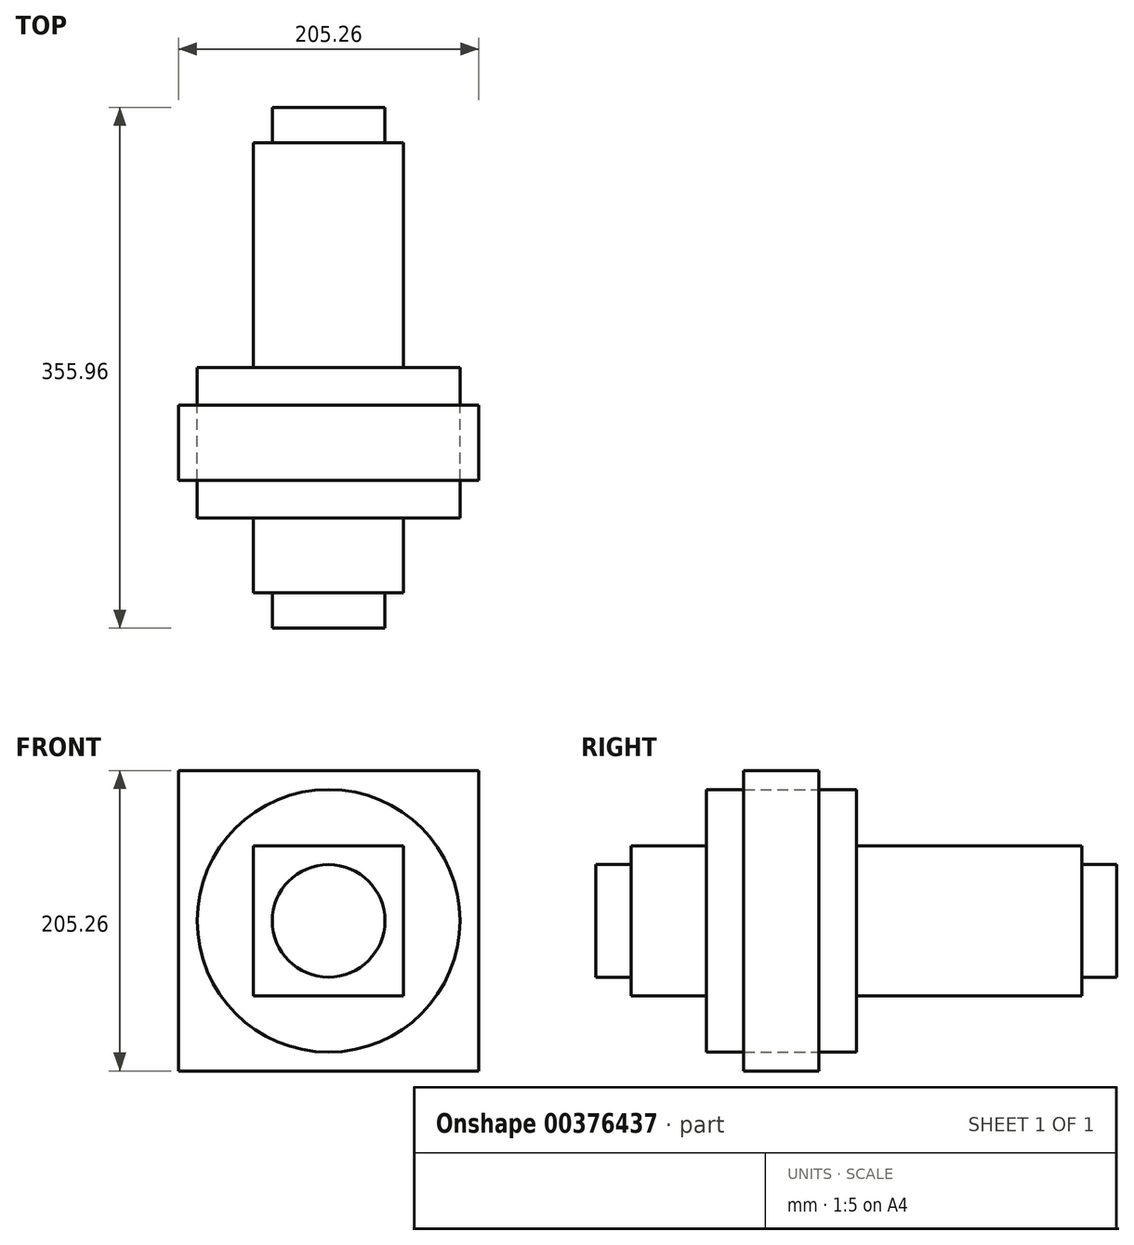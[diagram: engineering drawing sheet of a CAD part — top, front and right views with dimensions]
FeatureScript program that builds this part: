
annotation { "Feature Type Name" : "Feature", "Feature Type Description" : "" }
export const myFeature = defineFeature(function(context is Context, id is Id, definition is map)
    precondition{}
    {
        {
            var Q0;
            Q0=qCreatedBy(makeId("Front.planeOp"),FACE);
            var sketch = newSketch(context, id + "F0", { "sketchPlane" : qUnion([Q0])});
            skLineSegment(sketch, "E0.bottom", {"start": v(102.63, -102.63) * mm, "end": v(-102.63, -102.63) * mm});
            skLineSegment(sketch, "E0.top", {"start": v(102.63, 102.63) * mm, "end": v(-102.63, 102.63) * mm});
            skLineSegment(sketch, "E0.left", {"start": v(102.63, -102.63) * mm, "end": v(102.63, 102.63) * mm});
            skLineSegment(sketch, "E0.right", {"start": v(-102.63, -102.63) * mm, "end": v(-102.63, 102.63) * mm});
            skPoint(sketch, "E0.middle", {"position": v(0, 0) * mm});
            skCircle(sketch, "E1", {"center": v(0, 0) * mm, "radius": 89.8 * mm});
            skSolve(sketch);
        }
        {
            var Q0;
            Q0=qSketchRegion(id+"F0",true);
            extrude(context, id + "F1", {"entities" : qUnion([Q0]), "endBound" : BoundingType.SYMMETRIC, "depth" : 51.31 * mm});
        }
        {
            var Q0;
            Q0=makeQuery(id+"F0.imprint","IMPRINT",FACE,{"disambiguationData":[TD([[makeQuery(id+"F0.imprint","IMPRINT",EDGE,{"derivedFrom":sQuery(id+"F0.wireOp",EDGE,"E1")}),1.0]])]});
            extrude(context, id + "F2", {"entities" : qUnion([Q0]), "endBound" : BoundingType.SYMMETRIC, "depth" : 102.62 * mm});
        }
        {
            var Q0;
            Q0=makeQuery(id+"F2.opExtrude","CAP_FACE",FACE,{"disambiguationData":[OSD([sQuery(id+"F0.wireOp",EDGE,"E1")])],"isStart":true});
            var sketch = newSketch(context, id + "F3", { "sketchPlane" : qUnion([Q0])});
            skLineSegment(sketch, "E2.bottom", {"start": v(51.3, -51.3) * mm, "end": v(-51.3, -51.3) * mm});
            skLineSegment(sketch, "E2.top", {"start": v(51.3, 51.3) * mm, "end": v(-51.3, 51.3) * mm});
            skLineSegment(sketch, "E2.left", {"start": v(51.3, -51.3) * mm, "end": v(51.3, 51.3) * mm});
            skLineSegment(sketch, "E2.right", {"start": v(-51.3, -51.3) * mm, "end": v(-51.3, 51.3) * mm});
            skPoint(sketch, "E2.middle", {"position": v(0, 0) * mm});
            skCircle(sketch, "E3", {"center": v(0, 0) * mm, "radius": 38.5 * mm});
            skSolve(sketch);
        }
        {
            var Q0;
            Q0=makeQuery(id+"F3.imprint","IMPRINT",FACE,{"disambiguationData":[TD([[makeQuery(id+"F3.imprint","IMPRINT",EDGE,{"derivedFrom":sQuery(id+"F3.wireOp",EDGE,"E2.bottom")}),-1.0]])]});
            extrude(context, id + "F4", {"entities" : qUnion([Q0]), "operationType" : NewBodyOperationType.ADD, "endBound" : BoundingType.SYMMETRIC, "depth" : 307.85 * mm});
        }
        {
            var Q0;
            Q0=makeQuery(id+"F4.boolean.opBoolean","SPLIT",FACE,{"disambiguationData":[TD([makeQuery(id+"F4.opExtrude","SWEPT_FACE",FACE,{"disambiguationData":[OSD([sQuery(id+"F3.wireOp",EDGE,"E3")])]})])],"derivedFrom":makeQuery(id+"F2.opExtrude","CAP_FACE",FACE,{"disambiguationData":[OSD([sQuery(id+"F0.wireOp",EDGE,"E1")])],"isStart":true})});
            extrude(context, id + "F5", {"entities" : qUnion([Q0]), "operationType" : NewBodyOperationType.ADD, "endBound" : BoundingType.SYMMETRIC, "depth" : 355.96 * mm});
        }
    });
